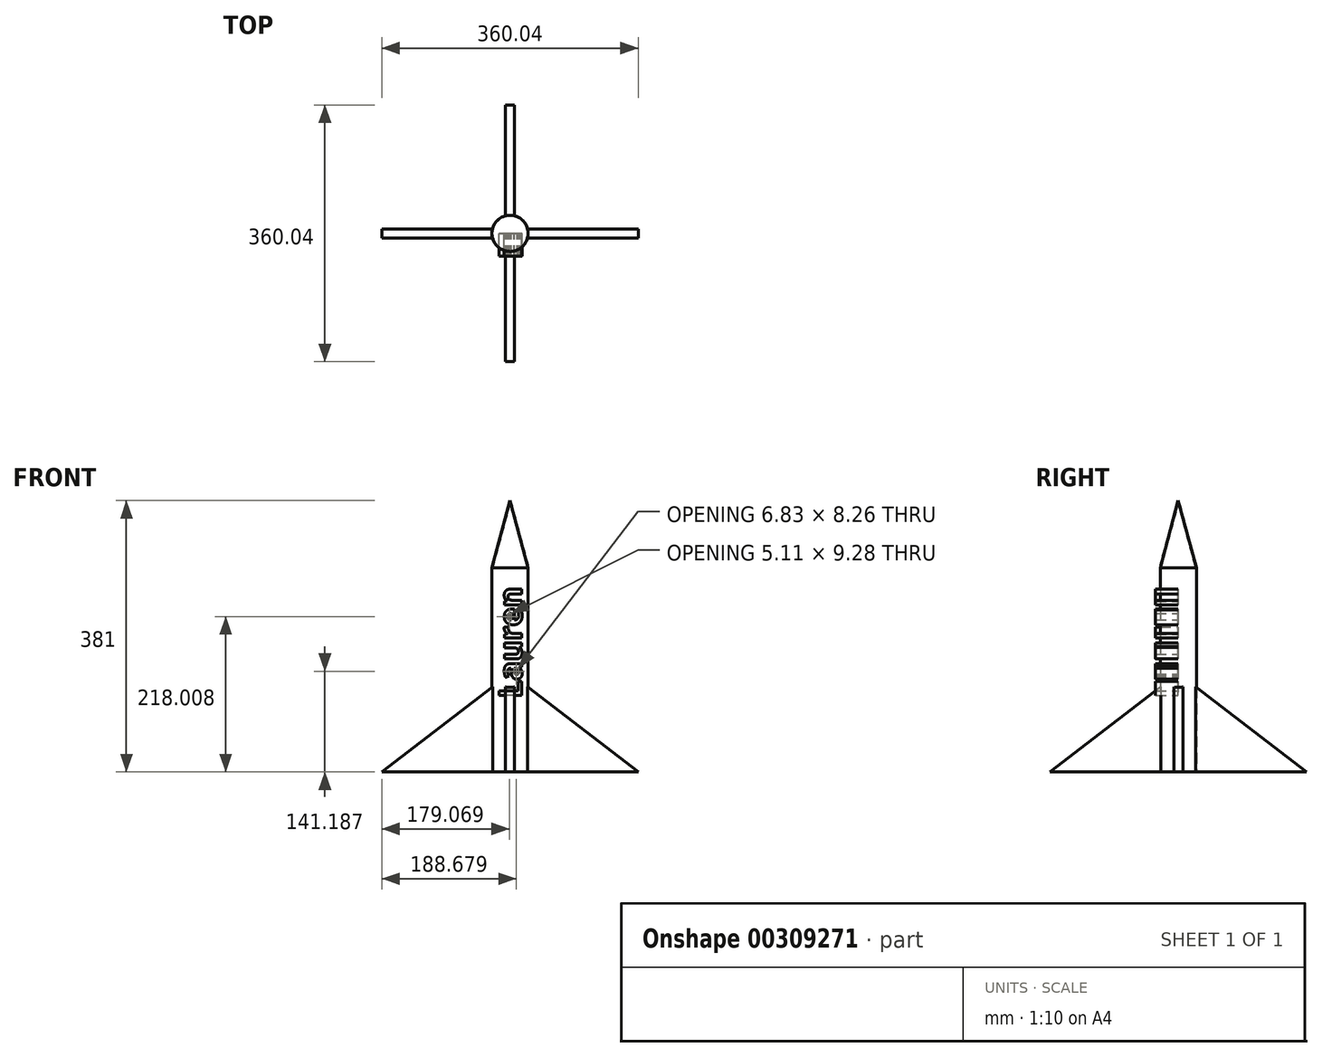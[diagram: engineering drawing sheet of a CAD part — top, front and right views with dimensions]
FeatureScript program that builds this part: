
annotation { "Feature Type Name" : "Feature", "Feature Type Description" : "" }
export const myFeature = defineFeature(function(context is Context, id is Id, definition is map)
    precondition{}
    {
        {
            var Q0;
            Q0=qCreatedBy(makeId("Top.planeOp"),FACE);
            var sketch = newSketch(context, id + "F0", { "sketchPlane" : qUnion([Q0])});
            skCircle(sketch, "E0", {"center": v(0, 0) * mm, "radius": 25.4 * mm});
            skSolve(sketch);
        }
        {
            var Q0;
            Q0=qSketchRegion(id+"F0",true);
            extrude(context, id + "F1", {"entities" : qUnion([Q0]), "depth" : 381 * mm});
        }
        {
            var Q0;
            Q0=makeQuery(id+"F1.opExtrude","CAP_EDGE",EDGE,{"disambiguationData":[OSD([sQuery(id+"F0.wireOp",EDGE,"E0")])],"isStart":false});
            chamfer(context, id + "F2", {"entities" : qUnion([Q0]), "chamferType" : ChamferType.OFFSET_ANGLE, "width" : 25.4 * mm, "oppositeDirection" : false, "angle" : 75 * degree, "tangentPropagation" : true});
        }
        {
            var Q0;
            Q0=qCreatedBy(makeId("Front.planeOp"),FACE);
            var sketch = newSketch(context, id + "F3", { "sketchPlane" : qUnion([Q0])});
            skLineSegment(sketch, "E1", {"start": v(0, 138.23) * mm, "end": v(0, 0) * mm});
            skLineSegment(sketch, "E2", {"start": v(180.02, 0) * mm, "end": v(0, 0) * mm});
            skLineSegment(sketch, "E3", {"start": v(-129.4, 68.74) * mm, "end": v(-118.85, 63.14) * mm});
            skLineSegment(sketch, "E4", {"start": v(0, 138.23) * mm, "end": v(180.02, 0) * mm});
            skSolve(sketch);
        }
        {
            var Q0;
            Q0=qSketchRegion(id+"F3",true);
            extrude(context, id + "F4", {"entities" : qUnion([Q0]), "operationType" : NewBodyOperationType.ADD, "endBound" : BoundingType.SYMMETRIC, "depth" : 12.7 * mm});
        }
        {
            var Q0;
            Q0=makeQuery(id+"F1.opExtrude","SWEPT_BODY",BODY,{"disambiguationData":[OSD([sQuery(id+"F0.wireOp",EDGE,"E0")])]});
            var Q1;
            Q1=makeQuery(id+"F1.opExtrude","SWEPT_FACE",FACE,{"disambiguationData":[OSD([sQuery(id+"F0.wireOp",EDGE,"E0")])]});
            circularPattern(context, id + "F5", {"entities" : qUnion([Q0]), "axis" : qUnion([Q1]), "angle" : 360 * degree, "instanceCount" : 4, "equalSpace" : true});
        }
        {
            var Q0;
            Q0=qCreatedBy(makeId("Front.planeOp"),FACE);
            var sketch = newSketch(context, id + "F6", { "sketchPlane" : qUnion([Q0])});
            skText(sketch, "E5", { "text": "Lauren", "fontName": "OpenSans-Bold.ttf"});
            const initialGuessF6  = {"E5": [0.01647, 0.10334, 0, 1, 0.03195]};
            skSetInitialGuess(sketch, initialGuessF6);
            skSolve(sketch);
        }
        {
            var Q0;
            Q0 = qSketchRegion(id + "F6", true);
            extrude(context, id + "F7", {"entities" : qUnion([Q0]), "depth" : 31.75 * mm});
        }
    });
